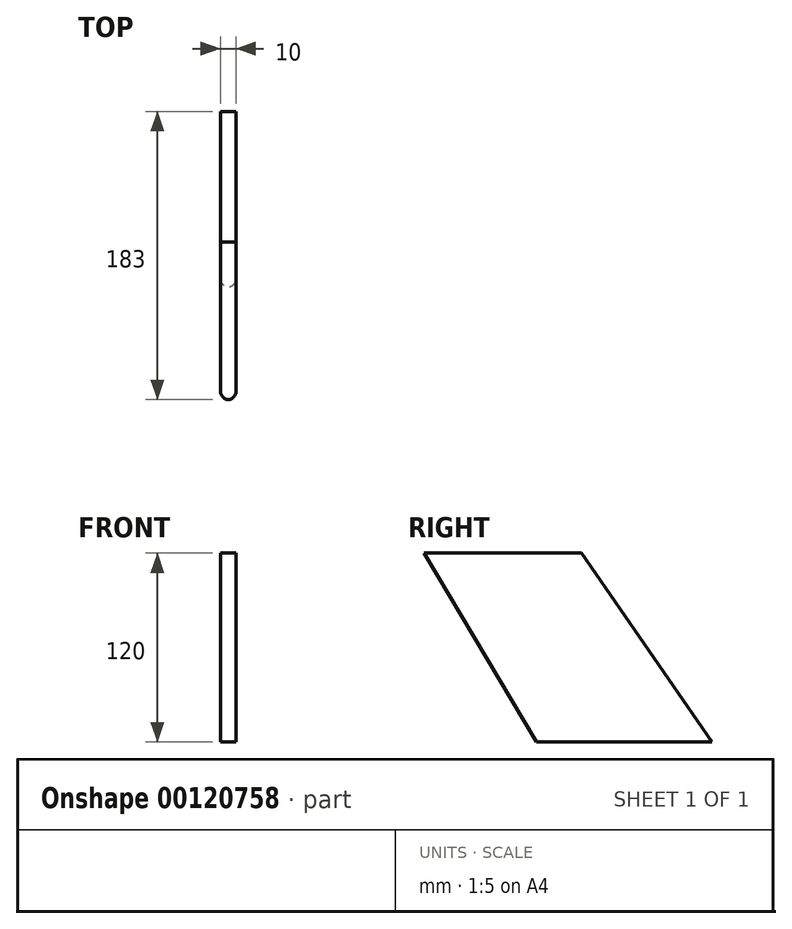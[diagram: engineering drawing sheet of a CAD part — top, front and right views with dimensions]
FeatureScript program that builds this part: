
annotation { "Feature Type Name" : "Feature", "Feature Type Description" : "" }
export const myFeature = defineFeature(function(context is Context, id is Id, definition is map)
    precondition{}
    {
        {
            var Q0;
            Q0=qCreatedBy(makeId("Right.planeOp"),FACE);
            var sketch = newSketch(context, id + "F0", { "sketchPlane" : qUnion([Q0])});
            skLineSegment(sketch, "E0", {"start": v(0, 0) * mm, "end": v(-71.46, 120) * mm});
            skLineSegment(sketch, "E1", {"start": v(-71.46, 120) * mm, "end": v(28.54, 120) * mm});
            skLineSegment(sketch, "E2", {"start": v(28.54, 120) * mm, "end": v(111.54, 0) * mm});
            skLineSegment(sketch, "E3", {"start": v(111.54, 0) * mm, "end": v(0, 0) * mm});
            skLineSegment(sketch, "E4", {"start": v(0, 0) * mm, "end": v(0, 120) * mm});
            skSolve(sketch);
        }
        {
            var Q0;
            Q0 = qSketchRegion(id + "F0", true);
            extrude(context, id + "F1", {"entities" : qUnion([Q0]), "depth" : 10 * mm});
        }
        {
            var Q0;
            Q0=makeQuery(id+"F1.opExtrude","CAP_EDGE",EDGE,{"disambiguationData":[OSD([sQuery(id+"F0.wireOp",EDGE,"E0")])],"isStart":true});
            var Q1;
            Q1=makeQuery(id+"F1.opExtrude","CAP_EDGE",EDGE,{"disambiguationData":[OSD([sQuery(id+"F0.wireOp",EDGE,"E0")])],"isStart":false});
            fillet(context, id + "F2", {"entities" : qUnion([Q0, Q1]), "radius" : 5 * mm, "tangentPropagation" : true, "allowEdgeOverflow" : false});
        }
    });
